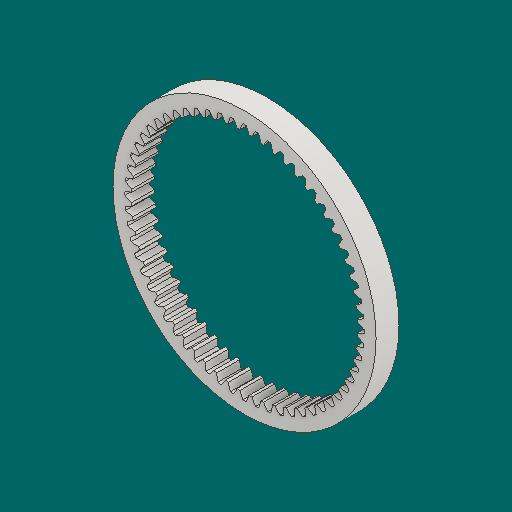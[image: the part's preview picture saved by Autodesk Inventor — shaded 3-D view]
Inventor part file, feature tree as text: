
AUTODESK INVENTOR PART (.ipt)
format: ipt  version: 2023.1 (Build 271208000, 208)  size: 446,976 bytes
history: native  units: in
note: dims shown in document units (in); Inventor stores cm internally (conversion verified against a paired STEP export)
features: other x12, plane x3, sketch x2
ambient origin geometry x8: Origin, YZ Plane, XZ Plane, XY Plane, X Axis, Y Axis, Z Axis, Center Point
bodies: Solid1 (feature_tree)
feature tree (17):
  other  "Spur Gear2"
  other  "Solid1::Spur Gear2"
  other  "TaggingFeature1"
  sketch  "Sketch1"  dims[d0=0.3937in]
  sketch  "Sketch2"  dims[d9=0.0in d14=0.0in d15=1.05in d16=0.0in d17=0.0in d18=0.0in d19=1.05in]
  plane  "XZ Plane_1"
  plane  "Work Plane2"
  plane  "Work Plane3"
  other  "Srf1"
  other  "Srf1::Derived"
  other  "Start plane iMate"
  other  "Distance iMate"
  other  "Mesh iMate"
  other  "Position iMate"
  other  "Axis iMate"
  other  "Mesh iMate2"
  other  "Align iMate"
